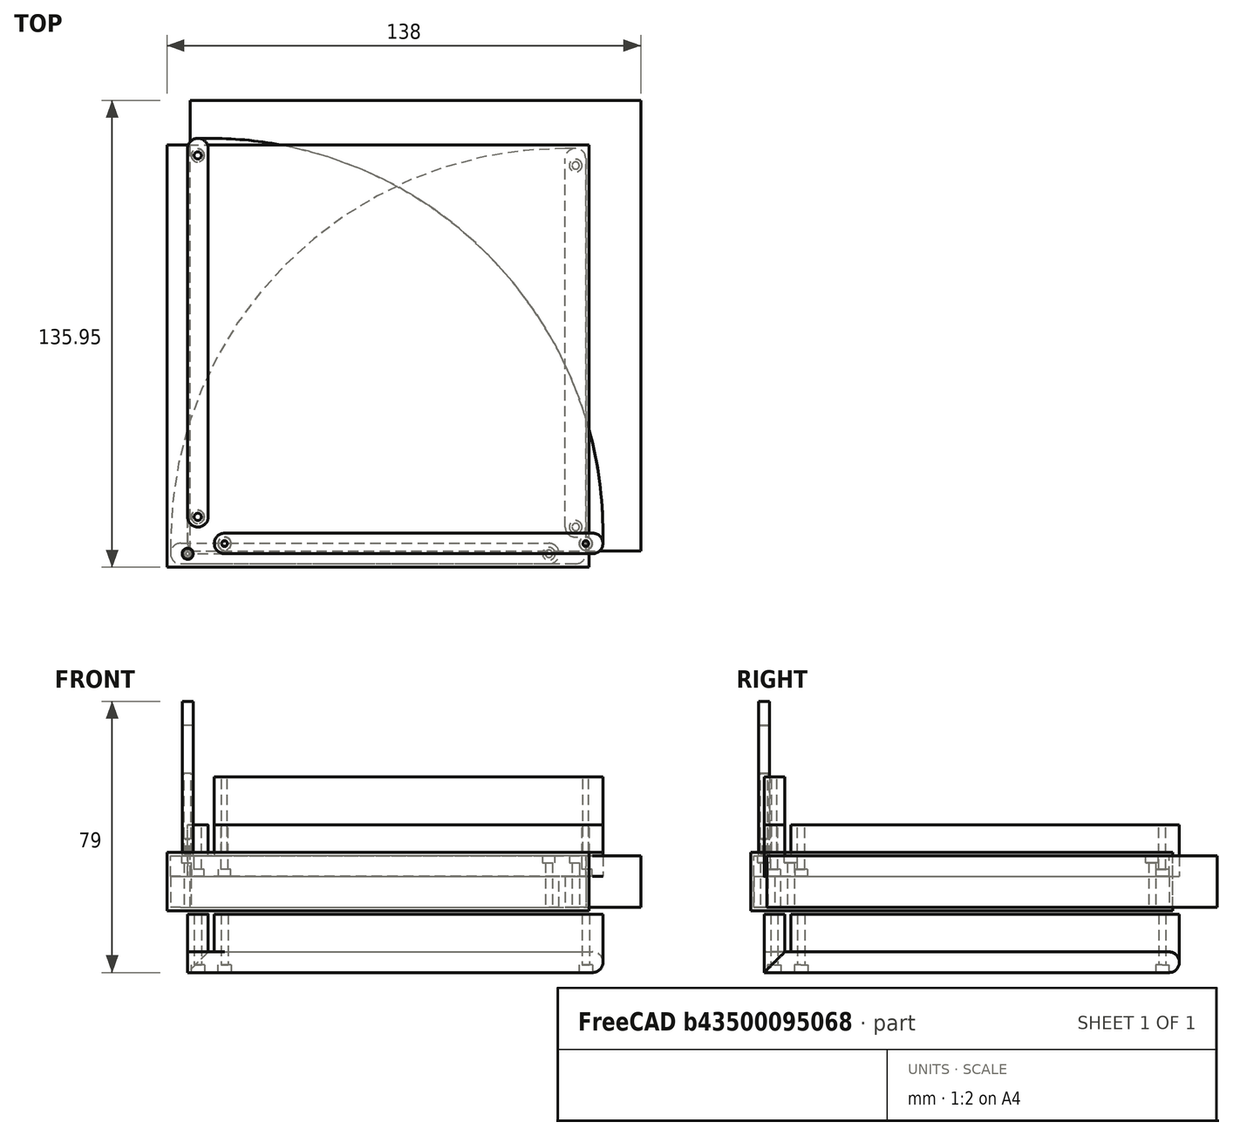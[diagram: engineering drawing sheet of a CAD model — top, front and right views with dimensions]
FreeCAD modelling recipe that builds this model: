
FCSTD DOCUMENT  (FreeCAD 1.1R20251125 (Git shallow))
Label: coffee-filter-holder-bamboo
License: All rights reserved
LicenseURL: https://en.wikipedia.org/wiki/All_rights_reserved
objects: Path::FeaturePython×9, App::Point×8, Sketcher::SketchObject×7, App::FeaturePython×7, Part::FeaturePython×7, App::DocumentObjectGroup×6, TechDraw::DrawViewDimension×5, PartDesign::Body×4, App::Part×3, PartDesign::Revolution×3, TechDraw::DrawProjGroupItem×3, Part::Feature×2, PartDesign::Pad×2, PartDesign::Pocket×2, App::Link×2, PartDesign::SubShapeBinder×1, Assembly::JointGroup×1, Assembly::AssemblyObject×1, TechDraw::DrawSVGTemplate×1, TechDraw::DrawProjGroup×1, +2 more types
note: 58 computed .brp shape members not serialized (recipe doc carries the construction recipe); baked Part::Feature solids carry a one-line shape summary decoded from their .brp

FEATURE [Part::Feature] Part__Feature  label="spanner"
  Placement = pos=(0,0,40) rot=(0,0,1;0rad)
  shape: bbox 113.2 x 6 x 22 mm, 11 faces (baked)
FEATURE [App::Point] Origin001
  Role = Origin
FEATURE [App::Point] Origin002
  Role = Origin
FEATURE [Part::Feature] Part__Feature001  label="sidewall-right"
  shape: bbox 130.5 x 130.5 x 17 mm, 43 faces (baked)
FEATURE [App::Part] Part001  label="Side Wall Template"
  Group = -> [Part__Feature001]
  Origin = -> Origin003
FEATURE [App::Point] Origin007  label="Origin008"
  Role = Origin
FEATURE [App::Point] Origin009  label="Origin011"
  Role = Origin
FEATURE [PartDesign::SubShapeBinder] Binder
  BindCopyOnChange = 0
  BindMode = 0
  ClaimChildren = false
  Context = -> Part002 [Body.Binder.]
  Fuse = false
  MakeFace = true
  OffsetFill = false
  OffsetIntersection = false
  OffsetJoinType = 0
  OffsetOpenResult = false
  PartialLoad = false
  Refine = true
  Relative = true
  Support = -> [Part001[Part__Feature001.]]
  _Version = 2
FEATURE [Sketcher::SketchObject] Sketch
  ArcFitTolerance = 1e-06
  AttachmentSupport = -> [Origin008]
  ExternalGeometry = -> [Binder]
  ExternalTypes = [0,0,0,0]
  FullyConstrained = true
  MakeInternals = false
  MapMode = 5
  sketch-geometry (4):
    g0: LineSegment StartX=121 StartY=6 StartZ=0 EndX=121 EndY=3 EndZ=0
    g1: LineSegment StartX=3 StartY=0 StartZ=0 EndX=10.7782 EndY=0 EndZ=0
    g2: LineSegment StartX=0 StartY=3 StartZ=0 EndX=0 EndY=10.7782 EndZ=0
    g3: LineSegment StartX=3 StartY=121 StartZ=0 EndX=6 EndY=121 EndZ=0
  constraints (8):
    c: Coincident(g0,g-3)
    c: Coincident(g0,g-11)
    c: Coincident(g1,g-4)
    c: Coincident(g1,g-14)
    c: Coincident(g2,g-4)
    c: Coincident(g2,g-24)
    c: Coincident(g3,g-22)
    c: Coincident(g3,g-3)
FEATURE [PartDesign::Pad] Pad  label="Base Shape"
  Direction = (0,0,1)
  Length = -6
  Length2 = 10
  Profile = -> Sketch
  ReferenceAxis = -> Sketch [N_Axis]
  Refine = true
  SideType = 0
  Suppressed = false
  Type = 0
  Type2 = 0
FEATURE [Sketcher::SketchObject] Sketch001
  ArcFitTolerance = 1e-06
  AttachmentSupport = -> [Pad]
  ExternalGeometry = -> [Binder]
  ExternalTypes = [0,0]
  FullyConstrained = true
  MakeInternals = false
  MapMode = 5
FEATURE [PartDesign::Pad] Pad001  label="Ribs"
  BaseFeature = -> Pad
  Direction = (0,0,1)
  Length = 9
  Length2 = 10
  Profile = -> Sketch001
  ReferenceAxis = -> Sketch001 [N_Axis]
  Refine = true
  SideType = 0
  Suppressed = false
  Type = 0
  Type2 = 0
FEATURE [Sketcher::SketchObject] Sketch002
  ArcFitTolerance = 1e-06
  AttachmentSupport = -> [Pad001]
  ExternalGeometry = -> [Pad001]
  ExternalTypes = [0,0,0,0]
  FullyConstrained = true
  MakeInternals = false
  MapMode = 5
  Placement = pos=(0,0,9) rot=(0,0,1;0rad)
FEATURE [PartDesign::Pocket] Pocket001  label="Through Holes"
  BaseFeature = -> Pad001
  Direction = (0,0,-1)
  Length = 41
  Length2 = 5
  Profile = -> Sketch002
  ReferenceAxis = -> Sketch002 [N_Axis]
  Refine = true
  SideType = 0
  Suppressed = false
  Type = 0
  Type2 = 0
FEATURE [Sketcher::SketchObject] Sketch003
  ArcFitTolerance = 1e-06
  AttachmentSupport = -> [Pocket001]
  ExternalGeometry = -> [Pocket001]
  ExternalTypes = [0,0,0,0]
  FullyConstrained = true
  MakeInternals = false
  MapMode = 5
  Placement = pos=(0,0,-6) rot=(1,0,0;3.14159rad)
  sketch-geometry (4):
    g0: Circle CenterX=116 CenterY=-2.95 CenterZ=0 NormalX=0 NormalY=0 NormalZ=1 AngleXU=0 Radius=1.85
    g1: Circle CenterX=10.75 CenterY=-2.95 CenterZ=0 NormalX=0 NormalY=0 NormalZ=1 AngleXU=0 Radius=1.85
    g2: Circle CenterX=2.95 CenterY=-10.75 CenterZ=0 NormalX=0 NormalY=0 NormalZ=1 AngleXU=0 Radius=1.85
    g3: Circle CenterX=2.95 CenterY=-116 CenterZ=0 NormalX=0 NormalY=0 NormalZ=1 AngleXU=0 Radius=1.85
  constraints (8):
    c: Coincident(g0,g-5)
    c: Coincident(g1,g-8)
    c: Coincident(g2,g-11)
    c: Coincident(g3,g-14)
    c: Equal(g0,g1)
    c: Equal(g3,g2)
    c: Equal(g2,g1)
    c: Diameter(g0) = 3.7
FEATURE [PartDesign::Pocket] Pocket
  BaseFeature = -> Pocket001
  Direction = (0,0,1)
  Length = 2
  Length2 = 5
  Profile = -> Sketch003
  ReferenceAxis = -> Sketch003 [N_Axis]
  Refine = true
  SideType = 0
  Suppressed = false
  Type = 0
  Type2 = 0
FEATURE [PartDesign::Body] Body
  AllowCompound = false
  Group = -> [Sketch,Binder,Pad,Sketch001,Pad001,Sketch002,Pocket001,Sketch003,Pocket]
  Origin = -> Origin008
  Tip = -> Pocket
FEATURE [App::Part] Part002  label="Side Wall"
  Group = -> [Body]
  Origin = -> Origin006
FEATURE [App::Point] Origin011  label="Origin013"
  Role = Origin
FEATURE [App::Link] Spanner  label="Spanner001"
  LinkedObject = -> Part
FEATURE [App::FeaturePython] GroundedJoint  label="GroundedJoint001"  # Assembly grounded joint (typed FeaturePython)
  ObjectToGround = -> Spanner
FEATURE [App::Link] Side_Wall  label="Side Wall001"
  LinkPlacement = pos=(-0.0500095,-0.0499714,-8) rot=(0,0,1;0rad)
  LinkedObject = -> Part002
  Placement = pos=(-0.0500095,-0.0499714,-8) rot=(0,0,1;0rad)
FEATURE [App::FeaturePython] Joint  label="Distance001"  # Assembly joint (typed FeaturePython)
  Angle = 0
  AngleMax = 0
  AngleMin = 0
  Detach1 = false
  Detach2 = false
  Distance = 0
  Distance2 = 0
  EnableAngleMax = false
  EnableAngleMin = false
  EnableLengthMax = false
  EnableLengthMin = false
  JointType = 5 (Distance)
  LengthMax = 0
  LengthMin = 0
  Placement1 = pos=(64.3997,3.00052,9) rot=(0,0,1;0rad)
  Placement2 = pos=(64.3952,3.0003,-39) rot=(0,1,0;3.14159rad)
  Reference1 = -> Assembly [Side_Wall.Body.Face22,Side_Wall.Body.Face22]
  Reference2 = -> Assembly [Spanner.Part__Feature.Face4,Spanner.Part__Feature.Vertex4]
  Suppressed = false
FEATURE [Assembly::JointGroup] Joints
  Group = -> [GroundedJoint,Joint]
FEATURE [Assembly::AssemblyObject] Assembly
  Group = -> [Joints,Spanner,GroundedJoint,Side_Wall,Joint]
  Origin = -> Origin010
  Type = Assembly
FEATURE [App::FeaturePython] SetupSheet  # Path/CAM operation (typed FeaturePython)
  ClearanceHeightExpression = OpStockZMax+SetupSheet.ClearanceHeightOffset
  ClearanceHeightOffset = 5
  CoolantMode = 0
  CoolantModes = None | Flood | Mist
  FinalDepthExpression = OpFinalDepth
  HorizRapid = 0
  SafeHeightExpression = OpStockZMax+SetupSheet.SafeHeightOffset
  SafeHeightOffset = 3
  StartDepthExpression = OpStartDepth
  StepDownExpression = OpToolDiameter
  VertRapid = 0
FEATURE [Part::FeaturePython] Clone  label="Model-Side Wall"  # Draft clone (typed FeaturePython)
  AttacherType = Attacher::AttachEngine3D
  ForceCompound = false
  Fuse = false
  Objects = -> [Part002]
  PathResource = Model
  Placement = pos=(1,1,-9) rot=(0,0,1;0rad)
  Scale = (1,1,1)
FEATURE [App::DocumentObjectGroup] Model
  Group = -> [Clone]
FEATURE [App::FeaturePython] PropertyBag001  label="Attributes001"  # WARN: FeaturePython — macro-defined, semantics opaque (R4)
  CustomPropertyGroups = 0
  CuttingEdgeHeight = 25
  Diameter = 3.175
  Flutes = 4
  Length = 45
  ShankDiameter = 3.175
FEATURE [Sketcher::SketchObject] Sketch005
  ArcFitTolerance = 0
  AttachmentSupport = -> [XZ_Plane007]
  ExternalTypes = [0]
  FullyConstrained = true
  MakeInternals = false
  MapMode = 5
  Placement = pos=(0,0,0) rot=(1,0,0;1.5708rad)
  expr: Constraints[10] = <<Attributes001>>.Length
  expr: Constraints[16] = <<Attributes001>>.ShankDiameter
  expr: Constraints[18] = <<Attributes001>>.CuttingEdgeHeight
  expr: Constraints[9] = <<Attributes001>>.Diameter
  sketch-geometry (8):
    g0: LineSegment StartX=0 StartY=45 StartZ=0 EndX=0 EndY=0 EndZ=0
    g1: LineSegment StartX=0 StartY=0 StartZ=0 EndX=1.5875 EndY=0 EndZ=0
    g2: LineSegment StartX=1.5875 StartY=0 StartZ=0 EndX=1.5875 EndY=25 EndZ=0
    g3: LineSegment StartX=1.5875 StartY=45 StartZ=0 EndX=0 EndY=45 EndZ=0
    g4: LineSegment [constr] StartX=1.5875 StartY=0 StartZ=0 EndX=-1.5875 EndY=0 EndZ=0
    g5: LineSegment StartX=1.5875 StartY=24.99 StartZ=0 EndX=1.5875 EndY=25 EndZ=0
    g6: LineSegment StartX=1.5875 StartY=45 StartZ=0 EndX=1.5875 EndY=24.99 EndZ=0
    g7: LineSegment [constr] StartX=-1.5875 StartY=45 StartZ=0 EndX=1.5875 EndY=45 EndZ=0
  constraints (21):
    c: Vertical(g0)
    c: Coincident(g0,g1)
    c: Horizontal(g1)
    c: Coincident(g1,g2)
    c: Vertical(g2)
    c: Horizontal(g3)
    c: Coincident(g0,g3)
    c: Coincident(g4,g1)
    c: Symmetric(g1,g4,g0)
    c: DistanceX(g4,g4) = 3.175
    c: DistanceY(g2,g3) = 45
    c: Coincident(g2,g5)
    c: Vertical(g6)
    c: Coincident(g3,g6)
    c: Symmetric(g7,g7,g0)
    c: Coincident(g7,g3)
    c: DistanceX(g7,g7) = 3.175
    c: Coincident(g5,g6)
    c: DistanceY(g2) = 25
    c: Coincident(g0,g-1)
    c: DistanceY(g5,g2) = 0.01
FEATURE [PartDesign::Revolution] Revolution001
  AllowMultiFace = false
  Angle = 360
  Angle2 = 60
  Axis = (0,2e-16,1)
  Base = (0,0,0)
  Placement = pos=(0,0,0) rot=(1,0,0;1.5708rad)
  Profile = -> Sketch005
  ReferenceAxis = -> Sketch005 [V_Axis]
  Reversed = true
  Suppressed = false
  Type = 0
FEATURE [App::Point] Origin014  label="Origin017"
  Role = Origin
FEATURE [PartDesign::Body] Body002  label="Endmill002"
  AllowCompound = false
  Group = -> [Sketch005,Revolution001,PropertyBag001]
  Origin = -> Origin015
  Tip = -> Revolution001
FEATURE [Part::FeaturePython] _3_175mm_Endmill  label="3.175mm Endmill"  # WARN: FeaturePython — macro-defined, semantics opaque (R4)
  BitBody = -> Body002
  Chipload = 0
  CuttingEdgeHeight = 25
  Diameter = 3.175
  Flutes = 4
  Length = 45
  Material = 0
  ShankDiameter = 3.175
  ShapeID = endmill
  ShapeType = 6
  SpindleDirection = 0
  ToolBitID = 3.175mm_Endmill
FEATURE [Path::FeaturePython] _3_175mm_Endmill001  label="3.175mm Endmill001"  # Path/CAM operation (typed FeaturePython)
  HorizFeed = 16.6667
  HorizRapid = 0
  SpindleDir = 0
  SpindleSpeed = 0
  Tool = -> _3_175mm_Endmill
  ToolNumber = 2
  VertFeed = 16.6667
  VertRapid = 0
  expr: HorizRapid = SetupSheet.HorizRapid
  expr: VertRapid = SetupSheet.VertRapid
FEATURE [Path::FeaturePython] Adaptive  label="Adaptive - Main Pocket Clear"  # Path/CAM operation (typed FeaturePython)
  Active = true
  Base = -> [Clone]
  ClearanceHeight = 5
  CoolantMode = 0
  CycleTime = 03:56:20
  ExtensionCorners = true
  ExtensionFeature = -> [Clone]
  ExtensionLengthDefault = 3.25
  FinalDepth = -9
  FinishDepth = 0.2
  FinishingProfile = true
  ForceInsideOut = false
  HelixAngle = 5
  HelixConeAngle = 0
  HelixDiameterLimit = 0
  KeepToolDownRatio = 3
  LiftDistance = 0.5
  ModelAwareExperiment = false
  OpFinalDepth = -9
  OpStartDepth = 0
  OpStockZMax = 0
  OpStockZMin = -15
  OpToolDiameter = 3.175
  OperationType = 0
  OrderCutsByRegion = false
  SafeHeight = 3
  Side = 1
  StartDepth = 0
  StepDown = 1
  StepOver = 30
  StockToLeave = 0
  StopProcessing = false
  Stopped = false
  Tolerance = 0.1
  ToolController = -> _3_175mm_Endmill001
  UseHelixArcs = false
  UseOutline = true
  ZStockToLeave = 0
  expr: ClearanceHeight = OpStockZMax + SetupSheet.ClearanceHeightOffset
  expr: ExtensionLengthDefault = 3.25
  expr: FinalDepth = OpFinalDepth
  expr: SafeHeight = OpStockZMax + SetupSheet.SafeHeightOffset
  expr: StartDepth = OpStartDepth
  expr: StepDown = 1
FEATURE [Path::FeaturePython] Adaptive002  label="Adaptive - External Profile"  # Path/CAM operation (typed FeaturePython)
  Active = true
  Base = -> [Clone]
  ClearanceHeight = 5
  CoolantMode = 0
  CycleTime = 00:58:03
  ExtensionCorners = true
  ExtensionLengthDefault = 1.5875
  FinalDepth = -15.1
  FinishDepth = 0
  FinishingProfile = true
  ForceInsideOut = true
  HelixAngle = 5
  HelixConeAngle = 0
  HelixDiameterLimit = 0
  KeepToolDownRatio = 3
  LiftDistance = 0.5
  ModelAwareExperiment = false
  OpFinalDepth = -15
  OpStartDepth = 0
  OpStockZMax = 0
  OpStockZMin = -15
  OpToolDiameter = 3.175
  OperationType = 1
  OrderCutsByRegion = false
  SafeHeight = 3
  Side = 0
  StartDepth = 0
  StepDown = 1.5
  StepOver = 40
  StockToLeave = 0
  StopProcessing = false
  Stopped = false
  Tolerance = 0.1
  ToolController = -> _3_175mm_Endmill001
  UseHelixArcs = false
  UseOutline = true
  ZStockToLeave = 0
  expr: ClearanceHeight = OpStockZMax + SetupSheet.ClearanceHeightOffset
  expr: ExtensionLengthDefault = OpToolDiameter / 2
  expr: FinalDepth = -15.1
  expr: SafeHeight = OpStockZMax + SetupSheet.SafeHeightOffset
  expr: StartDepth = OpStartDepth
  expr: StepDown = 1.5
FEATURE [App::FeaturePython] PropertyBag  label="Attributes010"  # WARN: FeaturePython — macro-defined, semantics opaque (R4)
  CustomPropertyGroups = 0
  Diameter = 2.1
  Flutes = 2
  Length = 24
  TipAngle = 119
FEATURE [Sketcher::SketchObject] Sketch006
  ArcFitTolerance = 0
  AttachmentSupport = -> [XZ_Plane008]
  ExternalTypes = [0]
  FullyConstrained = true
  MakeInternals = false
  MapMode = 5
  Placement = pos=(0,0,0) rot=(1,0,0;1.5708rad)
  expr: Constraints[13] = <<Attributes010>>.TipAngle
  expr: Constraints[14] = <<Attributes010>>.Diameter
  expr: Constraints[15] = <<Attributes010>>.Length
  sketch-geometry (7):
    g0: LineSegment StartX=0 StartY=24 StartZ=0 EndX=0 EndY=6.04e-14 EndZ=0
    g1: LineSegment StartX=0 StartY=6.04e-14 StartZ=0 EndX=1.05 EndY=0.618497 EndZ=0
    g2: LineSegment StartX=1.05 StartY=0.618497 StartZ=0 EndX=1.05 EndY=24 EndZ=0
    g3: LineSegment StartX=1.05 StartY=24 StartZ=0 EndX=0 EndY=24 EndZ=0
    g4: LineSegment [constr] StartX=1.05 StartY=0.618497 StartZ=0 EndX=-1.05 EndY=0.618497 EndZ=0
    g5: LineSegment [constr] StartX=-1.05 StartY=0.618497 StartZ=0 EndX=0 EndY=6.04e-14 EndZ=0
    g6: LineSegment [constr] StartX=0 StartY=6.04e-14 StartZ=0 EndX=1.05 EndY=0.618497 EndZ=0
  constraints (17):
    c: Vertical(g0)
    c: Coincident(g0,g1)
    c: Coincident(g1,g2)
    c: Vertical(g2)
    c: Coincident(g2,g3)
    c: Horizontal(g3)
    c: Coincident(g0,g3)
    c: Coincident(g4,g5)
    c: Coincident(g5,g6)
    c: Coincident(g6,g4)
    c: Coincident(g1,g4)
    c: Coincident(g5,g0)
    c: Symmetric(g4,g1,g0)
    c: Angle(g1,g5) = 2.07694
    c: DistanceX(g4,g4) = 2.1
    c: DistanceY(g0,g0) = 24
    c: Coincident(g0,g-1)
FEATURE [PartDesign::Revolution] Revolution
  AllowMultiFace = false
  Angle = 360
  Angle2 = 60
  Axis = (0,2e-16,1)
  Base = (0,0,0)
  Placement = pos=(0,0,0) rot=(1,0,0;1.5708rad)
  Profile = -> Sketch006
  ReferenceAxis = -> Sketch006 [V_Axis]
  Reversed = true
  Suppressed = false
  Type = 0
FEATURE [App::Point] Origin016
  Role = Origin
FEATURE [PartDesign::Body] Body003  label="Drill"
  AllowCompound = false
  Group = -> [Sketch006,Revolution,PropertyBag]
  Origin = -> Origin017
  Tip = -> Revolution
FEATURE [Part::FeaturePython] _2_1mm_Drill  label="2.1mm Drill"  # WARN: FeaturePython — macro-defined, semantics opaque (R4)
  BitBody = -> Body003
  Chipload = 0
  Diameter = 2.1
  Flutes = 2
  Length = 24
  Material = 0
  ShapeID = drill
  ShapeType = 5
  SpindleDirection = 0
  TipAngle = 119
  ToolBitID = 29946cca-a2d4-40a4-9766-5e803b813994
FEATURE [Path::FeaturePython] _2_1mm_Drill001  label="2.1mm Drill001"  # Path/CAM operation (typed FeaturePython)
  HorizFeed = 16.6667
  HorizRapid = 0
  SpindleDir = 0
  SpindleSpeed = 0
  Tool = -> _2_1mm_Drill
  ToolNumber = 3
  VertFeed = 8.33333
  VertRapid = 0
  expr: HorizRapid = SetupSheet.HorizRapid
  expr: VertRapid = SetupSheet.VertRapid
FEATURE [App::DocumentObjectGroup] Tools
  Group = -> [_3_175mm_Endmill001,_2_1mm_Drill001]
FEATURE [Path::FeaturePython] Drilling  label="Drilling002"  # Path/CAM operation (typed FeaturePython)
  Active = true
  AddTipLength = false
  Base = -> [Clone]
  ClearanceHeight = 5
  CoolantMode = 0
  CycleTime = 00:00:20
  DwellEnabled = false
  DwellTime = 1
  ExtraOffset = 1
  FinalDepth = -15
  KeepToolDown = false
  OpFinalDepth = -13
  OpStartDepth = 0
  OpStockZMax = 0
  OpStockZMin = -15
  OpToolDiameter = 2.1
  PeckDepth = 1.575
  PeckEnabled = true
  RetractHeight = 3
  RetractMode = 0
  SafeHeight = 3
  StartDepth = 0
  ToolController = -> _2_1mm_Drill001
  chipBreakEnabled = false
  feedRetractEnabled = false
  expr: ClearanceHeight = OpStockZMax + SetupSheet.ClearanceHeightOffset
  expr: FinalDepth = -15
  expr: PeckDepth = OpToolDiameter * 0.75
  expr: RetractHeight = StartDepth + SetupSheet.SafeHeightOffset
  expr: SafeHeight = OpStockZMax + SetupSheet.SafeHeightOffset
  expr: StartDepth = OpStartDepth
FEATURE [App::DocumentObjectGroup] Operations
  Group = -> [Adaptive,Adaptive002,Drilling]
FEATURE [App::FeaturePython] SetupSheet001  label="SetupSheet003"  # Path/CAM operation (typed FeaturePython)
  ClearanceHeightExpression = OpStockZMax+SetupSheet001.ClearanceHeightOffset
  ClearanceHeightOffset = 5
  CoolantMode = 0
  CoolantModes = None | Flood | Mist
  FinalDepthExpression = OpFinalDepth
  HorizRapid = 0
  SafeHeightExpression = OpStockZMax+SetupSheet001.SafeHeightOffset
  SafeHeightOffset = 3
  StartDepthExpression = OpStartDepth
  StepDownExpression = OpToolDiameter
  VertRapid = 0
FEATURE [Part::FeaturePython] Clone001  label="Model-Model-Side Wall001"  # Draft clone (typed FeaturePython)
  AttacherType = Attacher::AttachEngine3D
  ForceCompound = false
  Fuse = false
  Objects = -> [Clone]
  PathResource = Model
  Placement = pos=(116,-2.95,-6) rot=(0,-1,0;3.14159rad)
  Scale = (1,1,1)
FEATURE [App::DocumentObjectGroup] Model001
  Group = -> [Clone001]
FEATURE [Part::FeaturePython] Stock008  label="Stock012"  # WARN: FeaturePython — macro-defined, semantics opaque (R4)
  Base = -> Model001
  ExtXneg = 1
  ExtXpos = 1
  ExtYneg = 1
  ExtYpos = 1
  ExtZneg = 1
  ExtZpos = 1
  Placement = pos=(-5,-2.95,-15) rot=(0,0,1;0rad)
  StockType = FromBase
FEATURE [App::FeaturePython] PropertyBag003  label="Attributes012"  # WARN: FeaturePython — macro-defined, semantics opaque (R4)
  CustomPropertyGroups = 0
  CuttingEdgeHeight = 5
  Diameter = 1
  Flutes = 2
  Length = 38
  ShankDiameter = 3.17
FEATURE [Sketcher::SketchObject] Sketch008
  ArcFitTolerance = 0
  AttachmentSupport = -> [XZ_Plane010]
  ExternalTypes = [0]
  FullyConstrained = true
  MakeInternals = false
  MapMode = 5
  Placement = pos=(0,0,0) rot=(1,0,0;1.5708rad)
  expr: Constraints[10] = <<Attributes012>>.Length
  expr: Constraints[16] = <<Attributes012>>.ShankDiameter
  expr: Constraints[18] = <<Attributes012>>.CuttingEdgeHeight
  expr: Constraints[9] = <<Attributes012>>.Diameter
  sketch-geometry (8):
    g0: LineSegment StartX=0 StartY=38 StartZ=0 EndX=0 EndY=0 EndZ=0
    g1: LineSegment StartX=0 StartY=0 StartZ=0 EndX=0.5 EndY=0 EndZ=0
    g2: LineSegment StartX=0.5 StartY=0 StartZ=0 EndX=0.5 EndY=5 EndZ=0
    g3: LineSegment StartX=1.585 StartY=38 StartZ=0 EndX=0 EndY=38 EndZ=0
    g4: LineSegment [constr] StartX=0.5 StartY=0 StartZ=0 EndX=-0.5 EndY=0 EndZ=0
    g5: LineSegment StartX=1.585 StartY=4.99 StartZ=0 EndX=0.5 EndY=5 EndZ=0
    g6: LineSegment StartX=1.585 StartY=38 StartZ=0 EndX=1.585 EndY=4.99 EndZ=0
    g7: LineSegment [constr] StartX=-1.585 StartY=38 StartZ=0 EndX=1.585 EndY=38 EndZ=0
  constraints (21):
    c: Vertical(g0)
    c: Coincident(g0,g1)
    c: Horizontal(g1)
    c: Coincident(g1,g2)
    c: Vertical(g2)
    c: Horizontal(g3)
    c: Coincident(g0,g3)
    c: Coincident(g4,g1)
    c: Symmetric(g1,g4,g0)
    c: DistanceX(g4,g4) = 1
    c: DistanceY(g2,g3) = 38
    c: Coincident(g2,g5)
    c: Vertical(g6)
    c: Coincident(g3,g6)
    c: Symmetric(g7,g7,g0)
    c: Coincident(g7,g3)
    c: DistanceX(g7,g7) = 3.17
    c: Coincident(g5,g6)
    c: DistanceY(g2) = 5
    c: Coincident(g0,g-1)
    c: DistanceY(g5,g2) = 0.01
FEATURE [PartDesign::Revolution] Revolution003
  AllowMultiFace = false
  Angle = 360
  Angle2 = 60
  Axis = (0,2e-16,1)
  Base = (0,0,0)
  Placement = pos=(0,0,0) rot=(1,0,0;1.5708rad)
  Profile = -> Sketch008
  ReferenceAxis = -> Sketch008 [V_Axis]
  Reversed = true
  Suppressed = false
  Type = 0
FEATURE [App::Point] Origin020  label="Origin022"
  Role = Origin
FEATURE [PartDesign::Body] Body005  label="Endmill004"
  AllowCompound = false
  Group = -> [Sketch008,Revolution003,PropertyBag003]
  Origin = -> Origin021
  Tip = -> Revolution003
FEATURE [Part::FeaturePython] _1_0mm_End_Mill_PN57  label="1.0mm End Mill-PN57"  # WARN: FeaturePython — macro-defined, semantics opaque (R4)
  BitBody = -> Body005
  Chipload = 0
  CuttingEdgeHeight = 5
  Diameter = 1
  Flutes = 2
  Length = 38
  Material = 0
  ShankDiameter = 3.17
  ShapeID = endmill
  ShapeType = 6
  SpindleDirection = 0
  ToolBitID = a0aa9b30-c322-43e3-a153-4cfdf17ba31a
FEATURE [Path::FeaturePython] _1_0mm_End_Mill_PN001  label="1.0mm End Mill-PN001"  # Path/CAM operation (typed FeaturePython)
  HorizFeed = 5
  HorizRapid = 0
  SpindleDir = 0
  SpindleSpeed = 0
  Tool = -> _1_0mm_End_Mill_PN57
  ToolNumber = 2
  VertFeed = 5
  VertRapid = 0
  expr: HorizRapid = SetupSheet001.HorizRapid
  expr: VertRapid = SetupSheet001.VertRapid
FEATURE [App::DocumentObjectGroup] Tools001
  Group = -> [_1_0mm_End_Mill_PN001]
FEATURE [Path::FeaturePython] Helix  label="Counterbore001"  # Path/CAM operation (typed FeaturePython)
  Active = true
  Base = -> [Clone001]
  ClearanceHeight = 3
  CoolantMode = 0
  CutMode = 0
  CycleTime = Cycletime Error
  Direction = 1
  FinalDepth = -2
  OffsetExtra = 0
  OpFinalDepth = -2
  OpStartDepth = 1
  OpStockZMax = 1
  OpStockZMin = -16
  OpToolDiameter = 1
  SafeHeight = 3
  StartDepth = 1
  StartRadius = 0
  StartSide = 1
  StepDown = 0.5
  StepOver = 50
  ToolController = -> _1_0mm_End_Mill_PN001
  expr: ClearanceHeight = 3
  expr: FinalDepth = OpFinalDepth
  expr: SafeHeight = 3
  expr: StartDepth = OpStartDepth
  expr: StepDown = 0.5
FEATURE [App::DocumentObjectGroup] Operations001
  Group = -> [Helix]
FEATURE [Path::FeaturePython] Job001  label="Counterbore"  # Path/CAM operation (typed FeaturePython)
  CycleTime = 00:00:00
  Fixtures = G54
  GeometryTolerance = 0.01
  JobType = 0
  Model = -> Model001
  Operations = -> Operations001
  OrderOutputBy = 1
  PostProcessor = 12
  PostProcessorArgs = --translate_drill
  PostProcessorOutputFile = L:<userpath>/Projects/Coffee-Filter-Holder/cam-output/bamboo-15mm/Counterbore-1_0mm_End_Mill-PN_57.nc
  SetupSheet = -> SetupSheet001
  SplitOutput = false
  Stock = -> Stock008
  Tools = -> Tools001
FEATURE [Part::FeaturePython] Stock007  label="Stock011"  # WARN: FeaturePython — macro-defined, semantics opaque (R4)
  Base = -> Model
  ExtXneg = 0.25
  ExtXpos = 10
  ExtYneg = 0.25
  ExtYpos = 10
  ExtZneg = 0
  ExtZpos = 0
  Placement = pos=(1,1,-15) rot=(0,0,1;0rad)
  StockType = FromBase
FEATURE [Path::FeaturePython] Job  label="Milling"  # Path/CAM operation (typed FeaturePython)
  CycleTime = 04:54:43
  Fixtures = G54
  GeometryTolerance = 0.01
  JobType = 0
  Model = -> Model
  Operations = -> Operations
  OrderOutputBy = 1
  PostProcessor = 12
  PostProcessorArgs = --translate_drill --return-to=0,0
  PostProcessorOutputFile = L:<userpath>/Projects/Coffee-Filter-Holder/cam-output/milling-pocket-profile.nc
  SetupSheet = -> SetupSheet
  SplitOutput = true
  Stock = -> Stock007
  Tools = -> Tools
FEATURE [TechDraw::DrawSVGTemplate] Template
  EditableTexts = approval_person=B. Hecate; creator=D. Harriman; date_of_issue=28 Dec 2025; document_type=Component Drawing; drawing_number=CFH-01; general_tolerances=ISO 2768-m; language_code=EN; part_material=AL 6061-T6; revision_index=1; scale=1 : 1; sheet_number=1 / 1; title=Spanner
  Height = 210
  Orientation = 1
  Template = C:/Program Files/FreeCAD 1.1/data/Mod/TechDraw/Templates/ISO/A4_Landscape_ISO5457_minimal.svg
  Width = 297
FEATURE [TechDraw::DrawProjGroupItem] View  label="Front"
  CoarseView = false
  Direction = (0,-1,0)
  Focus = 100
  HardHidden = false
  IsoCount = 0
  IsoHidden = false
  IsoVisible = false
  LockPosition = true
  Perspective = false
  Rotation = 0
  RotationVector = (1,0,0)
  ScaleType = 2
  ScrubCount = 1
  SeamHidden = false
  SeamVisible = false
  SmoothHidden = false
  SmoothVisible = true
  Source = -> [Part__Feature]
  Type = 0
  X = 0
  XDirection = (1,0,0)
  Y = 0
FEATURE [TechDraw::DrawProjGroupItem] ProjItem  label="Bottom"
  CoarseView = false
  Direction = (0,0,-1)
  Focus = 100
  HardHidden = false
  IsoCount = 0
  IsoHidden = false
  IsoVisible = false
  LockPosition = false
  Perspective = false
  Rotation = 0
  RotationVector = (1,0,0)
  ScaleType = 0
  ScrubCount = 1
  SeamHidden = false
  SeamVisible = false
  SmoothHidden = false
  SmoothVisible = true
  Source = -> [Part__Feature]
  Type = 5
  X = 0
  XDirection = (1,0,0)
  Y = 58.3476
FEATURE [TechDraw::DrawProjGroupItem] ProjItem003  label="FrontTopRight"
  CoarseView = false
  Direction = (0.57735,-0.57735,0.57735)
  Focus = 100
  HardHidden = false
  IsoCount = 0
  IsoHidden = false
  IsoVisible = false
  LockPosition = false
  Perspective = false
  Rotation = 0
  RotationVector = (1,0,0)
  ScaleType = 0
  ScrubCount = 1
  SeamHidden = false
  SeamVisible = false
  SmoothHidden = false
  SmoothVisible = true
  Source = -> [Part__Feature]
  Type = 7
  X = -121.1
  XDirection = (0.707107,0.707107,0)
  Y = 36.415
FEATURE [TechDraw::DrawProjGroup] ProjGroup
  Anchor = -> View
  AutoDistribute = false
  LockPosition = false
  ProjectionType = 0
  Rotation = 0
  ScaleType = 0
  Source = -> [Part__Feature]
  Views = -> [View,ProjItem,ProjItem003]
  X = 191.718
  Y = 106.271
  spacingX = 15
  spacingY = 15
FEATURE [TechDraw::DrawViewDimension] Dimension001
  AngleOverride = false
  Arbitrary = false
  ArbitraryTolerances = false
  BoxCorners = (2) [(-56.6109,-11,-1e-07),(56.6109,11,1e-07)]
  EqualTolerance = true
  ExtensionAngle = 0
  FormatSpec = %.2w
  FormatSpecOverTolerance = %+.2w
  FormatSpecUnderTolerance = %+.2w
  Inverted = false
  LineAngle = 0
  LockPosition = false
  MeasureType = 1
  OverTolerance = 0
  References2D = -> [View]
  Rotation = 0
  ScaleType = 0
  ShowUnits = false
  TheoreticalExact = false
  Type = 0
  UnderTolerance = 0
  UseActualArea = true
  X = -4.3168
  Y = -30.4816
FEATURE [TechDraw::DrawViewDimension] Dimension
  AngleOverride = false
  Arbitrary = false
  ArbitraryTolerances = false
  BoxCorners = (2) [(-56.6109,-11,-1e-07),(56.6109,11,1e-07)]
  EqualTolerance = true
  ExtensionAngle = 0
  FormatSpec = %.2w
  FormatSpecOverTolerance = %+.2w
  FormatSpecUnderTolerance = %+.2w
  Inverted = false
  LineAngle = 0
  LockPosition = false
  MeasureType = 1
  OverTolerance = 0
  References2D = -> [View]
  Rotation = 0
  ScaleType = 0
  ShowUnits = false
  TheoreticalExact = false
  Type = 2
  UnderTolerance = 0
  UseActualArea = true
  X = 68.5934
  Y = 0
FEATURE [TechDraw::DrawViewDimension] Dimension002
  AngleOverride = false
  Arbitrary = false
  ArbitraryTolerances = false
  BoxCorners = (2) [(-56.6109,-3,0),(56.6109,3,0)]
  EqualTolerance = true
  ExtensionAngle = 0
  FormatSpec = R%.2w
  FormatSpecOverTolerance = %+.2w
  FormatSpecUnderTolerance = %+.2w
  Inverted = false
  LineAngle = 0
  LockPosition = false
  MeasureType = 1
  OverTolerance = 0
  References2D = -> [ProjItem]
  Rotation = 0
  ScaleType = 0
  ShowUnits = false
  TheoreticalExact = false
  Type = 4
  UnderTolerance = 0
  UseActualArea = true
  X = -70.3208
  Y = -4.17237
FEATURE [TechDraw::DrawViewDimension] Dimension003
  AngleOverride = false
  Arbitrary = false
  ArbitraryTolerances = false
  BoxCorners = (2) [(-56.6109,-3,0),(56.6109,3,0)]
  EqualTolerance = true
  ExtensionAngle = 0
  FormatSpec = ⌀%.2w
  FormatSpecOverTolerance = %+.2w
  FormatSpecUnderTolerance = %+.2w
  Inverted = false
  LineAngle = 0
  LockPosition = false
  MeasureType = 1
  OverTolerance = 0
  References2D = -> [ProjItem]
  Rotation = 0
  ScaleType = 0
  ShowUnits = false
  TheoreticalExact = false
  Type = 5
  UnderTolerance = 0
  UseActualArea = true
  X = -68.3222
  Y = 13.5538
FEATURE [TechDraw::DrawViewBalloon] Balloon
  BubbleShape = 7
  EndType = 0
  EndTypeScale = 1
  KinkLength = 5
  LockPosition = false
  OriginX = 51.6109
  OriginY = 0.85
  Rotation = 0
  ScaleType = 0
  ShapeScale = 1
  SourceView = -> ProjItem
  Text = 2x M2.0-0.4 ↧5.0
  TextWrapLen = -1
  X = 10.0444
  Y = 21.1063
FEATURE [TechDraw::DrawViewDimension] Dimension004
  AngleOverride = false
  Arbitrary = false
  ArbitraryTolerances = false
  BoxCorners = (2) [(-56.6109,-3,0),(56.6109,3,0)]
  EqualTolerance = true
  ExtensionAngle = 0
  FormatSpec = %.2w
  FormatSpecOverTolerance = %+.2w
  FormatSpecUnderTolerance = %+.2w
  Inverted = false
  LineAngle = 0
  LockPosition = false
  MeasureType = 1
  OverTolerance = 0
  References2D = -> [ProjItem]
  Rotation = 0
  ScaleType = 0
  ShowUnits = false
  TheoreticalExact = false
  Type = 0
  UnderTolerance = 0
  UseActualArea = true
  X = 65.4763
  Y = 0
FEATURE [TechDraw::DrawPage] Page
  KeepUpdated = true
  NextBalloonIndex = 2
  ProjectionType = 0
  Template = -> Template
  Views = -> [ProjGroup,Dimension001,Dimension,Dimension002,Dimension003,Balloon,Dimension004]
FEATURE [App::Part] Part  label="Spanner"
  Group = -> [Part__Feature,Page]
  Origin = -> Origin
